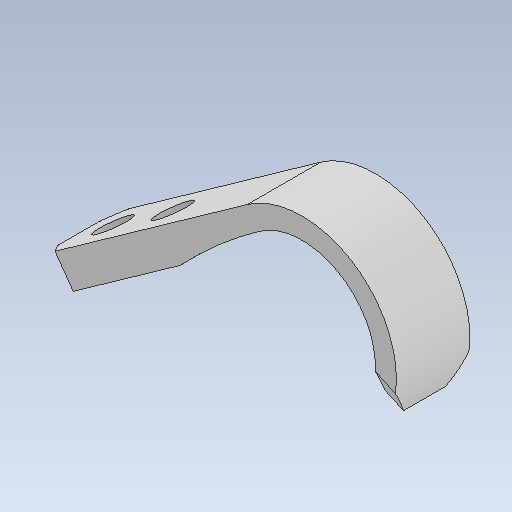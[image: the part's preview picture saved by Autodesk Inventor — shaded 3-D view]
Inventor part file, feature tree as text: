
AUTODESK INVENTOR PART (.ipt)
format: ipt  version: 2023 (Build 270158000, 158)  size: 151,552 bytes
history: native  units: mm
features: reference x4, sketch x3, extrude x3, other x3, chamfer x2, plane x1, projected_geometry x1
ambient origin geometry x8: Origin, YZ Plane, XZ Plane, XY Plane, X Axis, Y Axis, Z Axis, Center Point
bodies: Solid1 (feature_tree)
feature tree (17):
  sketch  "Sketch1"  dims[d0=3.0mm d1=3.0mm]
  plane  "Work Plane1"
  extrude  "Extrusion1"  Depth=3.0mm
  extrude  "Extrusion2"  Depth=18.0mm
  chamfer  "Chamfer1"  Distance=2.0mm
  extrude  "Extrusion3"  Depth=10.0mm
  chamfer  "Chamfer2"  Distance=7.0mm
  reference  "Reference1"
  reference  "Reference2"
  sketch  "Sketch2"  dims[d2=24.0mm d3=18.0mm]
  reference  "Reference3"
  reference  "Reference4"
  sketch  "Sketch3"  dims[d4=9.0mm d5=2.0mm d6=14.0mm d7=7.0mm d8=10.0mm d9=0.0mm d10=3.2mm d11=3.2mm d12=10.0mm d13=0.0mm d14=1.5mm d15=2.0mm d16=45.0deg d17=30.0deg d18=10.0mm d19=0.0mm d20=1.5mm d21=2.0mm d22=60.0deg]
  projected_geometry  "Projected Loop1"
  parser-record x1  (decoder bookkeeping rows leaked as tree rows — omitted from the tree; the rows remain in map.json)
  other  "leg_1.iam"
  other  "leg_link_1:1"
note: 1 file-system path scrubbed to <path> (originals preserved in map.json)
